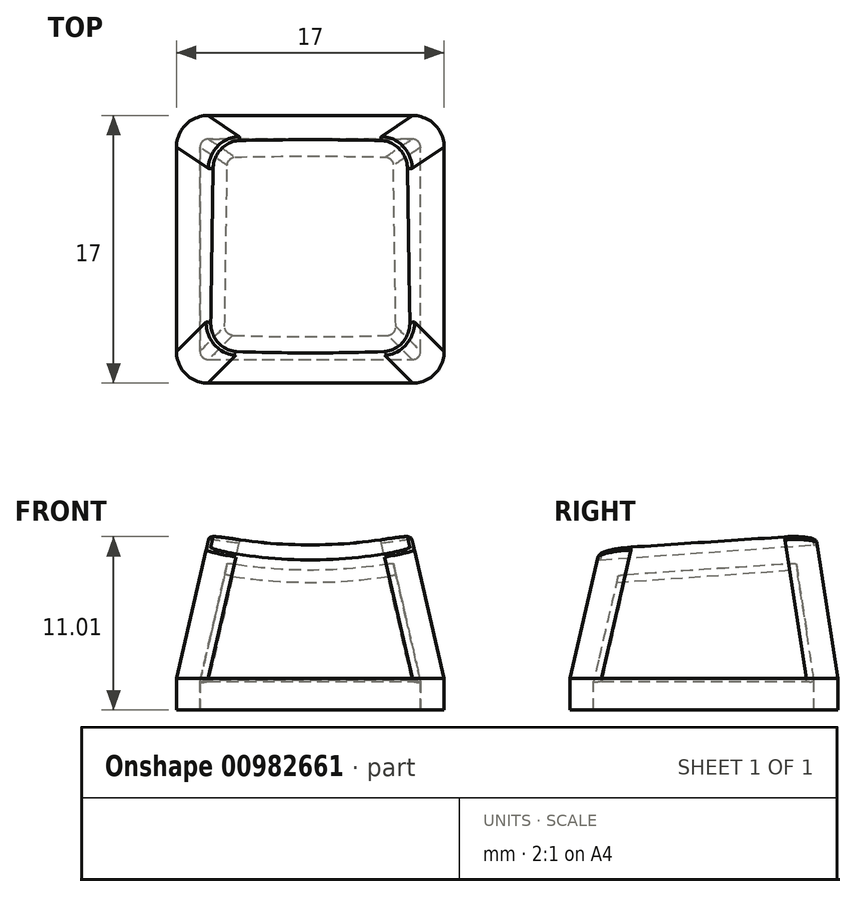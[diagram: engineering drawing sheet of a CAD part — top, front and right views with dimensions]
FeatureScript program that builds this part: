
annotation { "Feature Type Name" : "Feature", "Feature Type Description" : "" }
export const myFeature = defineFeature(function(context is Context, id is Id, definition is map)
    precondition{}
    {
        {
            assignVariable(context, id + "F0", {"name" : "Height", "anyValue" : 10 * mm});
        }
        {
            assignVariable(context, id + "F1", {"name" : "LoftHeight", "anyValue" : getVariable(context, 'Height') + 5 * mm});
        }
        {
            assignVariable(context, id + "F2", {"name" : "Slope", "anyValue" : 4 * degree});
        }
        {
            assignVariable(context, id + "F3", {"name" : "SkirtHeight", "anyValue" : 2 * mm});
        }
        {
            assignVariable(context, id + "F4", {"name" : "WallThickness", "anyValue" : 1.5 * mm});
        }
        {
            assignVariable(context, id + "F5", {"name" : "SharpEdgeBevelRadius", "anyValue" : .25 * mm});
        }
        {
            var Q0;
            Q0=qCreatedBy(makeId("Top.planeOp"),FACE);
            var sketch = newSketch(context, id + "F6", { "sketchPlane" : qUnion([Q0])});
            skLineSegment(sketch, "E0.bottom", {"start": v(-6.5, -8.5) * mm, "end": v(6.5, -8.5) * mm});
            skLineSegment(sketch, "E0.top", {"start": v(-6.5, 8.5) * mm, "end": v(6.5, 8.5) * mm});
            skLineSegment(sketch, "E0.left", {"start": v(-8.5, -6.5) * mm, "end": v(-8.5, 6.5) * mm});
            skLineSegment(sketch, "E0.right", {"start": v(8.5, -6.5) * mm, "end": v(8.5, 6.5) * mm});
            skPoint(sketch, "E0.middle", {"position": v(0, 0) * mm});
            skPoint(sketch, "E1.visualSharp", {"position": v(-8.5, 8.5) * mm});
            skArc(sketch, "E1.filletArc", {"start": v(-6.5, 8.5) * mm, "mid": v(-7.91, 7.91) * mm, "end": v(-8.5, 6.5) * mm});
            skPoint(sketch, "E2.visualSharp", {"position": v(8.5, 8.5) * mm});
            skArc(sketch, "E2.filletArc", {"start": v(8.5, 6.5) * mm, "mid": v(7.91, 7.91) * mm, "end": v(6.5, 8.5) * mm});
            skPoint(sketch, "E3.visualSharp", {"position": v(8.5, -8.5) * mm});
            skArc(sketch, "E3.filletArc", {"start": v(6.5, -8.5) * mm, "mid": v(7.91, -7.91) * mm, "end": v(8.5, -6.5) * mm});
            skPoint(sketch, "E4.visualSharp", {"position": v(-8.5, -8.5) * mm});
            skArc(sketch, "E4.filletArc", {"start": v(-8.5, -6.5) * mm, "mid": v(-7.91, -7.91) * mm, "end": v(-6.5, -8.5) * mm});
            skSolve(sketch);
        }
        {
            var Q0;
            Q0 = qSketchRegion(id + "F6", true);
            extrude(context, id + "F7", {"entities" : qUnion([Q0]), "depth" : getVariable(context, 'SkirtHeight'), "offsetDistance" : 25 * mm});
        }
        {
            var Q0;
            Q0=qCreatedBy(makeId("Top.planeOp"),FACE);
            cPlane(context, id + "F8", {"entities" : qUnion([Q0]), "cplaneType" : CPlaneType.OFFSET, "offset" : getVariable(context, 'LoftHeight'), "width" : 150 * mm, "height" : 150 * mm});
        }
        {
            var Q0;
            Q0=qCreatedBy(id+"F8.planeOp",FACE);
            var sketch = newSketch(context, id + "F9", { "sketchPlane" : qUnion([Q0])});
            skLineSegment(sketch, "E5.bottom", {"start": v(-3.5, -5.5) * mm, "end": v(3.5, -5.5) * mm});
            skLineSegment(sketch, "E5.top", {"start": v(-3.5, 6.5) * mm, "end": v(3.5, 6.5) * mm});
            skLineSegment(sketch, "E5.left", {"start": v(-5.5, -3.5) * mm, "end": v(-5.5, 4.5) * mm});
            skLineSegment(sketch, "E5.right", {"start": v(5.5, -3.5) * mm, "end": v(5.5, 4.5) * mm});
            skPoint(sketch, "E5.middle", {"position": v(0, 1) * mm});
            skPoint(sketch, "E6.visualSharp", {"position": v(-5.5, 6.5) * mm});
            skArc(sketch, "E6.filletArc", {"start": v(-3.5, 6.5) * mm, "mid": v(-4.91, 5.91) * mm, "end": v(-5.5, 4.5) * mm});
            skPoint(sketch, "E7.visualSharp", {"position": v(5.5, 6.5) * mm});
            skArc(sketch, "E7.filletArc", {"start": v(5.5, 4.5) * mm, "mid": v(4.91, 5.91) * mm, "end": v(3.5, 6.5) * mm});
            skPoint(sketch, "E8.visualSharp", {"position": v(5.5, -5.5) * mm});
            skArc(sketch, "E8.filletArc", {"start": v(3.5, -5.5) * mm, "mid": v(4.91, -4.91) * mm, "end": v(5.5, -3.5) * mm});
            skPoint(sketch, "E9.visualSharp", {"position": v(-5.5, -5.5) * mm});
            skArc(sketch, "E9.filletArc", {"start": v(-5.5, -3.5) * mm, "mid": v(-4.91, -4.91) * mm, "end": v(-3.5, -5.5) * mm});
            skSolve(sketch);
        }
        {
            var Q1;
            Q1=makeQuery(id+"F7.opExtrude","CAP_FACE",FACE,{"disambiguationData":[OSD([sQuery(id+"F6.wireOp",EDGE,"E0.bottom"),sQuery(id+"F6.wireOp",EDGE,"E0.top"),sQuery(id+"F6.wireOp",EDGE,"E0.left"),sQuery(id+"F6.wireOp",EDGE,"E0.right"),sQuery(id+"F6.wireOp",EDGE,"E1.filletArc"),sQuery(id+"F6.wireOp",EDGE,"E2.filletArc"),sQuery(id+"F6.wireOp",EDGE,"E3.filletArc"),sQuery(id+"F6.wireOp",EDGE,"E4.filletArc")])],"isStart":false});
            var Q2;
            Q2=makeQuery(id+"F9.imprint","IMPRINT",FACE,{"disambiguationData":[TD([[makeQuery(id+"F9.imprint","IMPRINT",EDGE,{"derivedFrom":sQuery(id+"F9.wireOp",EDGE,"E5.bottom")}),1.0]])]});
            loft(context, id + "F10", {"operationType" : NewBodyOperationType.ADD, "sheetProfilesArray" : [{ "sheetProfileEntities" : qUnion([Q1]) }, { "sheetProfileEntities" : qUnion([Q2]) }]});
        }
        {
            var Q0;
            Q0=qCreatedBy(makeId("Top.planeOp"),FACE);
            var sketch = newSketch(context, id + "F11", { "sketchPlane" : qUnion([Q0])});
            skLineSegment(sketch, "E10", {"start": v(-17.66, 19) * mm, "end": v(17.66, 19) * mm, "construction": true});
            skLineSegment(sketch, "E11", {"start": v(0, 0) * mm, "end": v(-17.66, 19) * mm, "construction": true});
            skLineSegment(sketch, "E12", {"start": v(0, 0) * mm, "end": v(17.66, 19) * mm, "construction": true});
            skLineSegment(sketch, "E13", {"start": v(0, 19) * mm, "end": v(0, 0) * mm, "construction": true});
            skSolve(sketch);
        }
        {
            var Q0;
            Q0=sQuery(id+"F11.wireOp",EDGE,"E10");
            cPlane(context, id + "F12", {"entities" : qUnion([Q0]), "cplaneType" : CPlaneType.LINE_ANGLE, "offset" : 25 * mm, "angle" : getVariable(context, 'Slope'), "width" : 150 * mm, "height" : 150 * mm});
        }
        {
            var Q0;
            Q0=qCreatedBy(id+"F12.planeOp",FACE);
            var sketch = newSketch(context, id + "F13", { "sketchPlane" : qUnion([Q0])});
            skLineSegment(sketch, "E14", {"start": v(0, -1.33) * mm, "end": v(0, 40.5) * mm, "construction": true});
            skCircle(sketch, "E15", {"center": v(0, 40.5) * mm, "radius": 30.53 * mm});
            skSolve(sketch);
        }
        {
            var Q0;
            Q0=makeQuery(id+"F13.imprint","IMPRINT",FACE,{"disambiguationData":[TD([[makeQuery(id+"F13.imprint","IMPRINT",EDGE,{"derivedFrom":sQuery(id+"F13.wireOp",EDGE,"E15")}),1.0]])]});
            extrude(context, id + "F14", {"entities" : qUnion([Q0]), "operationType" : NewBodyOperationType.REMOVE, "endBound" : BoundingType.THROUGH_ALL, "oppositeDirection" : true, "depth" : 20 * mm, "offsetDistance" : 25 * mm});
        }
        {
            var Q0;
            Q0=makeQuery(id+"F14.boolean.opBoolean","COPY",FACE,{"derivedFrom":makeQuery(id+"F14.opExtrude","SWEPT_FACE",FACE,{"disambiguationData":[OSD([sQuery(id+"F13.wireOp",EDGE,"E15")])]})});
            fillet(context, id + "F15", {"entities" : qUnion([Q0]), "radius" : getVariable(context, 'SharpEdgeBevelRadius'), "tangentPropagation" : true, "allowEdgeOverflow" : false});
        }
        {
            var Q0;
            Q0=makeQuery(id+"F7.opExtrude","CAP_FACE",FACE,{"disambiguationData":[OSD([sQuery(id+"F6.wireOp",EDGE,"E0.bottom"),sQuery(id+"F6.wireOp",EDGE,"E0.top"),sQuery(id+"F6.wireOp",EDGE,"E0.left"),sQuery(id+"F6.wireOp",EDGE,"E0.right"),sQuery(id+"F6.wireOp",EDGE,"E1.filletArc"),sQuery(id+"F6.wireOp",EDGE,"E2.filletArc"),sQuery(id+"F6.wireOp",EDGE,"E3.filletArc"),sQuery(id+"F6.wireOp",EDGE,"E4.filletArc")])],"isStart":true});
            shell(context, id + "F16", {"entities" : qUnion([Q0]), "thickness" : getVariable(context, 'WallThickness')});
        }
    });
